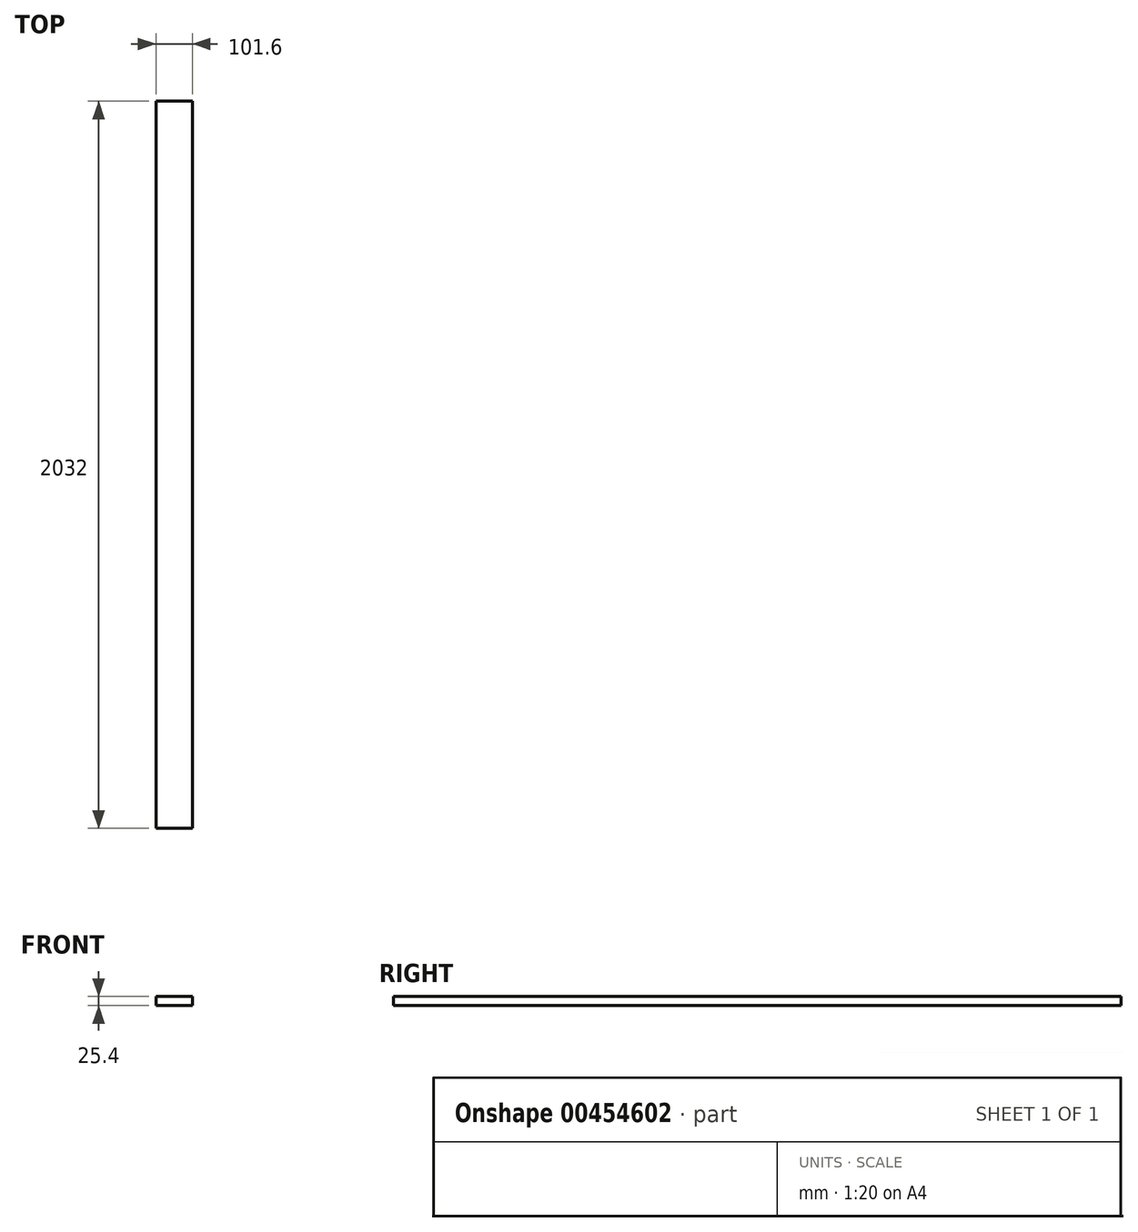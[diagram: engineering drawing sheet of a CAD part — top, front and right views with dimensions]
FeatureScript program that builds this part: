
annotation { "Feature Type Name" : "Feature", "Feature Type Description" : "" }
export const myFeature = defineFeature(function(context is Context, id is Id, definition is map)
    precondition{}
    {
        {
            var Q0;
            Q0=qCreatedBy(makeId("Front.planeOp"),FACE);
            var sketch = newSketch(context, id + "F0", { "sketchPlane" : qUnion([Q0])});
            skLineSegment(sketch, "E0.bottom", {"start": v(50.8, 12.7) * mm, "end": v(-50.8, 12.7) * mm});
            skLineSegment(sketch, "E0.top", {"start": v(50.8, -12.7) * mm, "end": v(-50.8, -12.7) * mm});
            skLineSegment(sketch, "E0.left", {"start": v(50.8, 12.7) * mm, "end": v(50.8, -12.7) * mm});
            skLineSegment(sketch, "E0.right", {"start": v(-50.8, 12.7) * mm, "end": v(-50.8, -12.7) * mm});
            skPoint(sketch, "E0.middle", {"position": v(0, 0) * mm});
            skSolve(sketch);
        }
        {
            var Q0;
            Q0=makeQuery(id+"F0.imprint","IMPRINT",FACE,{"disambiguationData":[TD([[makeQuery(id+"F0.imprint","IMPRINT",EDGE,{"derivedFrom":sQuery(id+"F0.wireOp",EDGE,"E0.bottom")}),1.0]])]});
            extrude(context, id + "F1", {"entities" : qUnion([Q0]), "depth" : 2032 * mm});
        }
    });
